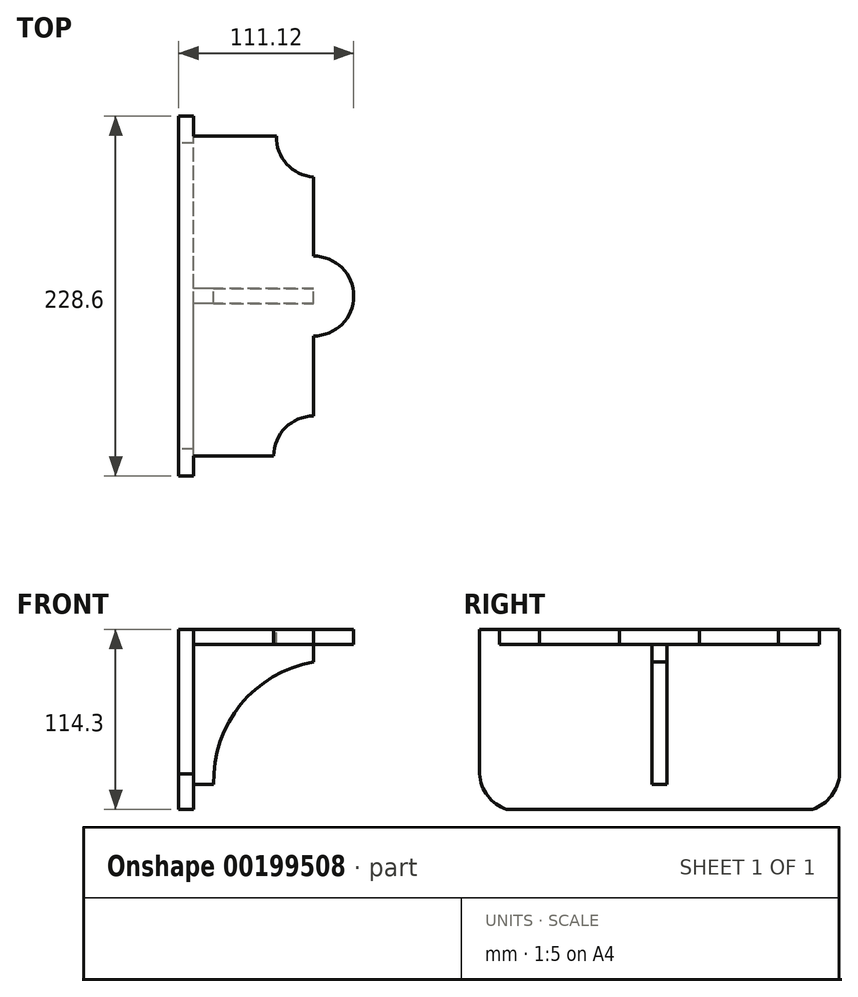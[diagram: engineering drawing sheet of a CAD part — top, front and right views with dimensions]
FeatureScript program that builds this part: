
annotation { "Feature Type Name" : "Feature", "Feature Type Description" : "" }
export const myFeature = defineFeature(function(context is Context, id is Id, definition is map)
    precondition{}
    {
        {
            var Q0;
            Q0=qCreatedBy(makeId("Right.planeOp"),FACE);
            var sketch = newSketch(context, id + "F0", { "sketchPlane" : qUnion([Q0])});
            skCircle(sketch, "E0", {"center": v(-124.94, 46.26) * mm, "radius": 10.4 * mm});
            skCircle(sketch, "E1", {"center": v(-124.94, 46.26) * mm, "radius": 31.75 * mm});
            skLineSegment(sketch, "E2", {"start": v(-122, 77.88) * mm, "end": v(-17.23, 77.88) * mm});
            skLineSegment(sketch, "E3", {"start": v(-118.16, 15.24) * mm, "end": v(-0.71, 15.24) * mm});
            skArc(sketch, "E4", {"start": v(-17.23, 77.88) * mm, "mid": v(-11.77, 60.6) * mm, "end": v(2.24, 49.13) * mm});
            skPoint(sketch, "E5.end.orphan", {"position": v(14.51, 77.88) * mm});
            skLineSegment(sketch, "E6", {"start": v(0.91, 49.73) * mm, "end": v(-0.71, 50.12) * mm});
            skLineSegment(sketch, "E7", {"start": v(-0.71, 50.12) * mm, "end": v(-0.71, 15.24) * mm});
            skPoint(sketch, "E8.orphan", {"position": v(-98.12, -71.85) * mm});
            skPoint(sketch, "E9", {"position": v(-37.66, -95.52) * mm});
            skLineSegment(sketch, "E10.bottom", {"start": v(-14.08, -27.06) * mm, "end": v(122.44, -27.06) * mm});
            skLineSegment(sketch, "E10.top", {"start": v(-14.08, -93.74) * mm, "end": v(122.44, -93.74) * mm});
            skLineSegment(sketch, "E10.left", {"start": v(-14.08, -27.06) * mm, "end": v(-14.08, -93.74) * mm});
            skLineSegment(sketch, "E10.right", {"start": v(122.44, -27.06) * mm, "end": v(122.44, -93.74) * mm});
            skArc(sketch, "E11", {"start": v(-98.28, -181.01) * mm, "mid": v(-129.26, -187.55) * mm, "end": v(-97.65, -185.78) * mm});
            skCircle(sketch, "E12", {"center": v(-113.52, -185.46) * mm, "radius": 31.75 * mm});
            skCircle(sketch, "E13", {"center": v(-37.32, -185.46) * mm, "radius": 11.11 * mm});
            skArc(sketch, "E14", {"start": v(-37.32, -210.86) * mm, "mid": v(-11.92, -185.46) * mm, "end": v(-37.32, -160.06) * mm});
            skLineSegment(sketch, "E15", {"start": v(-37.32, -160.06) * mm, "end": v(-94.47, -160.06) * mm});
            skLineSegment(sketch, "E16", {"start": v(-37.32, -210.86) * mm, "end": v(-94.47, -210.86) * mm});
            skLineSegment(sketch, "E17", {"start": v(-88.76, -181.01) * mm, "end": v(-98.28, -181.01) * mm});
            skLineSegment(sketch, "E18.MirrorCS", {"start": v(-88.76, -185.78) * mm, "end": v(-98.28, -185.78) * mm});
            skLineSegment(sketch, "E19", {"start": v(-88.76, -181.01) * mm, "end": v(-88.76, -185.78) * mm});
            skPoint(sketch, "E20.end.orphan", {"position": v(-40.1, -44.78) * mm});
            skPoint(sketch, "E20.start.orphan", {"position": v(-37.66, -44.78) * mm});
            skLineSegment(sketch, "E21", {"start": v(43.46, -93.74) * mm, "end": v(4.97, -27.06) * mm});
            skLineSegment(sketch, "E22", {"start": v(64.9, -93.74) * mm, "end": v(103.4, -27.06) * mm});
            skCircle(sketch, "E23", {"center": v(-494, 168.25) * mm, "radius": 73.03 * mm});
            skCircle(sketch, "E24", {"center": v(-494, 168.25) * mm, "radius": 38.1 * mm});
            skCircle(sketch, "E25", {"center": v(-494, 223.53) * mm, "radius": 7.94 * mm});
            skCircle(sketch, "E26", {"center": v(-530.58, 210.96) * mm, "radius": 7.94 * mm});
            skCircle(sketch, "E27", {"center": v(-550.67, 168.25) * mm, "radius": 7.94 * mm});
            skCircle(sketch, "E28", {"center": v(-528.76, 129.25) * mm, "radius": 7.94 * mm});
            skCircle(sketch, "E29.MirrorC", {"center": v(-457.4, 210.96) * mm, "radius": 7.94 * mm});
            skCircle(sketch, "E30.MirrorC", {"center": v(-437.33, 168.25) * mm, "radius": 7.94 * mm});
            skCircle(sketch, "E31.MirrorC", {"center": v(-459.23, 129.25) * mm, "radius": 7.94 * mm});
            skLineSegment(sketch, "E32.bottom", {"start": v(-629.68, -40.5) * mm, "end": v(-515.38, -40.5) * mm});
            skLineSegment(sketch, "E32.top", {"start": v(-629.68, -154.8) * mm, "end": v(-515.38, -154.8) * mm});
            skLineSegment(sketch, "E32.left", {"start": v(-629.68, -40.5) * mm, "end": v(-629.68, -154.8) * mm});
            skLineSegment(sketch, "E32.right", {"start": v(-515.38, -40.5) * mm, "end": v(-515.38, -154.8) * mm});
            skPoint(sketch, "E33", {"position": v(-515.38, -97.64) * mm});
            skPoint(sketch, "E34", {"position": v(-572.53, -40.5) * mm});
            skLineSegment(sketch, "E35", {"start": v(-572.53, -40.5) * mm, "end": v(-572.53, -154.8) * mm});
            skLineSegment(sketch, "E36", {"start": v(-515.38, -97.64) * mm, "end": v(-629.68, -97.64) * mm});
            skPoint(sketch, "E37.orphan", {"position": v(-629.68, -154.8) * mm});
            skPoint(sketch, "E38.MirrorCS.start.orphan", {"position": v(-515.38, -40.5) * mm});
            skPoint(sketch, "E39.MirrorCS.start.orphan", {"position": v(-515.38, -154.8) * mm});
            skLineSegment(sketch, "E40", {"start": v(-572.53, -59.48) * mm, "end": v(-610.7, -97.64) * mm});
            skLineSegment(sketch, "E41.MirrorCS", {"start": v(-572.53, -59.48) * mm, "end": v(-534.37, -97.64) * mm});
            skLineSegment(sketch, "E42.MirrorCS", {"start": v(-572.53, -135.81) * mm, "end": v(-610.7, -97.64) * mm});
            skLineSegment(sketch, "E43.MirrorCS", {"start": v(-572.53, -135.81) * mm, "end": v(-534.37, -97.64) * mm});
            skLineSegment(sketch, "E44", {"start": v(-515.38, -40.5) * mm, "end": v(-477.28, -62.5) * mm});
            skLineSegment(sketch, "E45", {"start": v(-477.28, -62.5) * mm, "end": v(-477.28, -81.14) * mm});
            skLineSegment(sketch, "E46", {"start": v(-477.28, -81.14) * mm, "end": v(-515.38, -81.14) * mm});
            skLineSegment(sketch, "E47", {"start": v(-477.28, -81.14) * mm, "end": v(-477.28, -26.83) * mm});
            skLineSegment(sketch, "E48.MirrorCS", {"start": v(-477.28, -114.15) * mm, "end": v(-515.38, -114.15) * mm});
            skLineSegment(sketch, "E49.MirrorCS", {"start": v(-515.38, -154.8) * mm, "end": v(-477.28, -132.8) * mm});
            skLineSegment(sketch, "E50.MirrorCS", {"start": v(-667.78, -81.14) * mm, "end": v(-629.68, -81.14) * mm});
            skLineSegment(sketch, "E51.MirrorCS", {"start": v(-629.68, -40.5) * mm, "end": v(-667.78, -62.5) * mm});
            skLineSegment(sketch, "E52.MirrorCS", {"start": v(-667.78, -81.14) * mm, "end": v(-667.78, -62.5) * mm});
            skLineSegment(sketch, "E53.MirrorCS", {"start": v(-667.78, -114.15) * mm, "end": v(-629.68, -114.15) * mm});
            skLineSegment(sketch, "E54.MirrorCS", {"start": v(-667.78, -114.45) * mm, "end": v(-667.78, -132.8) * mm});
            skLineSegment(sketch, "E55", {"start": v(-477.28, -114.15) * mm, "end": v(-477.28, -132.8) * mm});
            skLineSegment(sketch, "E56", {"start": v(-667.78, -132.8) * mm, "end": v(-629.68, -154.8) * mm});
            skLineSegment(sketch, "E57", {"start": v(-667.78, -114.15) * mm, "end": v(-667.78, -114.47) * mm});
            skLineSegment(sketch, "E58.bottom", {"start": v(-407.73, 102.8) * mm, "end": v(-279.92, 102.8) * mm});
            skLineSegment(sketch, "E58.top", {"start": v(-407.73, -11.5) * mm, "end": v(-279.92, -11.5) * mm});
            skLineSegment(sketch, "E58.left", {"start": v(-407.73, 102.8) * mm, "end": v(-407.73, -11.5) * mm});
            skLineSegment(sketch, "E58.right", {"start": v(-279.92, 102.8) * mm, "end": v(-279.92, -11.5) * mm});
            skLineSegment(sketch, "E59", {"start": v(-407.73, 102.8) * mm, "end": v(-440.64, 45.66) * mm});
            skLineSegment(sketch, "E60", {"start": v(-440.64, 45.66) * mm, "end": v(-407.73, -11.5) * mm});
            skLineSegment(sketch, "E61", {"start": v(-279.92, 102.8) * mm, "end": v(-250.14, 45.66) * mm});
            skLineSegment(sketch, "E62", {"start": v(-250.14, 45.66) * mm, "end": v(-279.92, -11.5) * mm});
            skLineSegment(sketch, "E63.bottom", {"start": v(-358.1, 115.5) * mm, "end": v(-326.34, 115.5) * mm});
            skLineSegment(sketch, "E63.top", {"start": v(-358.1, -24.2) * mm, "end": v(-326.34, -24.2) * mm});
            skLineSegment(sketch, "E63.left", {"start": v(-358.1, 115.5) * mm, "end": v(-358.1, -24.2) * mm});
            skLineSegment(sketch, "E63.right", {"start": v(-326.34, 115.5) * mm, "end": v(-326.34, -24.2) * mm});
            skLineSegment(sketch, "E64.bottom", {"start": v(-405.33, 64.7) * mm, "end": v(-351.35, 64.7) * mm});
            skLineSegment(sketch, "E64.top", {"start": v(-405.33, 26.6) * mm, "end": v(-351.35, 26.6) * mm});
            skLineSegment(sketch, "E64.left", {"start": v(-405.33, 64.7) * mm, "end": v(-405.33, 26.6) * mm});
            skLineSegment(sketch, "E64.right", {"start": v(-351.35, 64.7) * mm, "end": v(-351.35, 26.6) * mm});
            skLineSegment(sketch, "E65.MirrorCS", {"start": v(-285.46, 64.7) * mm, "end": v(-339.43, 64.7) * mm});
            skLineSegment(sketch, "E66.MirrorCS", {"start": v(-339.43, 64.7) * mm, "end": v(-339.43, 26.6) * mm});
            skLineSegment(sketch, "E67.MirrorCS", {"start": v(-285.46, 26.6) * mm, "end": v(-339.43, 26.6) * mm});
            skLineSegment(sketch, "E68.MirrorCS", {"start": v(-285.46, 64.7) * mm, "end": v(-285.46, 26.6) * mm});
            skLineSegment(sketch, "E69", {"start": v(-407.73, 102.8) * mm, "end": v(-397.88, 115.48) * mm});
            skLineSegment(sketch, "E70", {"start": v(-397.88, 115.48) * mm, "end": v(-389.84, 115.5) * mm});
            skLineSegment(sketch, "E71", {"start": v(-389.84, 115.5) * mm, "end": v(-389.84, 102.8) * mm});
            skLineSegment(sketch, "E72.MirrorCS", {"start": v(-300.94, 115.5) * mm, "end": v(-300.94, 102.8) * mm});
            skLineSegment(sketch, "E73.MirrorCS", {"start": v(-279.92, 102.8) * mm, "end": v(-292.62, 115.5) * mm});
            skLineSegment(sketch, "E74.MirrorCS", {"start": v(-292.62, 115.5) * mm, "end": v(-300.94, 115.5) * mm});
            skLineSegment(sketch, "E75.MirrorCS", {"start": v(-407.73, -11.5) * mm, "end": v(-397.99, -24.2) * mm});
            skLineSegment(sketch, "E76.MirrorCS", {"start": v(-397.99, -24.2) * mm, "end": v(-389.67, -24.2) * mm});
            skPoint(sketch, "E77", {"position": v(-326.34, 102.8) * mm});
            skLineSegment(sketch, "E78", {"start": v(-389.67, -24.2) * mm, "end": v(-389.67, -11.5) * mm});
            skPoint(sketch, "E79", {"position": v(-358.1, -11.5) * mm});
            skPoint(sketch, "E80.startSnap0", {"position": v(-342.22, 115.5) * mm});
            skLineSegment(sketch, "E81.MirrorCS", {"start": v(-286.45, -24.2) * mm, "end": v(-294.76, -24.2) * mm});
            skLineSegment(sketch, "E82.MirrorCS", {"start": v(-279.92, -11.5) * mm, "end": v(-286.45, -24.2) * mm});
            skLineSegment(sketch, "E83.MirrorCS", {"start": v(-294.76, -24.2) * mm, "end": v(-294.76, -11.5) * mm});
            skCircle(sketch, "E84", {"center": v(-850.31, 154.76) * mm, "radius": 63.5 * mm});
            skCircle(sketch, "E85", {"center": v(-850.31, 154.76) * mm, "radius": 44.45 * mm});
            skCircle(sketch, "E86", {"center": v(-926.51, 149.48) * mm, "radius": 40.81 * mm});
            skCircle(sketch, "E87.MirrorC", {"center": v(-774.11, 149.48) * mm, "radius": 40.81 * mm});
            skCircle(sketch, "E88", {"center": v(-926.51, 149.48) * mm, "radius": 12.7 * mm});
            skCircle(sketch, "E89.MirrorC", {"center": v(-774.11, 149.48) * mm, "radius": 12.7 * mm});
            skCircle(sketch, "E90", {"center": v(-503.59, -297.02) * mm, "radius": 19.05 * mm});
            skCircle(sketch, "E91", {"center": v(-503.59, -297.02) * mm, "radius": 31.75 * mm});
            skLineSegment(sketch, "E92", {"start": v(-503.59, -328.77) * mm, "end": v(-617.89, -328.77) * mm});
            skLineSegment(sketch, "E93", {"start": v(-503.59, -265.27) * mm, "end": v(-617.89, -265.27) * mm});
            skArc(sketch, "E94", {"start": v(-652.7, -239.87) * mm, "mid": v(-642.34, -262.23) * mm, "end": v(-617.89, -265.27) * mm});
            skArc(sketch, "E95.MirrorCS", {"start": v(-652.7, -354.17) * mm, "mid": v(-642.34, -331.81) * mm, "end": v(-617.89, -328.77) * mm});
            skLineSegment(sketch, "E96", {"start": v(-652.7, -239.87) * mm, "end": v(-672.55, -239.87) * mm});
            skLineSegment(sketch, "E97", {"start": v(-672.55, -239.87) * mm, "end": v(-680.33, -247.66) * mm});
            skLineSegment(sketch, "E98", {"start": v(-680.33, -247.66) * mm, "end": v(-680.33, -266.05) * mm});
            skLineSegment(sketch, "E99", {"start": v(-680.33, -247.66) * mm, "end": v(-680.33, -223.63) * mm});
            skLineSegment(sketch, "E100.MirrorCS", {"start": v(-680.33, -346.39) * mm, "end": v(-680.33, -328) * mm});
            skLineSegment(sketch, "E101.MirrorCS", {"start": v(-672.55, -354.17) * mm, "end": v(-680.33, -346.39) * mm});
            skLineSegment(sketch, "E102.MirrorCS", {"start": v(-652.7, -354.17) * mm, "end": v(-672.55, -354.17) * mm});
            skArc(sketch, "E103", {"start": v(-680.33, -328) * mm, "mid": v(-655.56, -297.02) * mm, "end": v(-680.33, -266.05) * mm});
            skCircle(sketch, "E104", {"center": v(-1098.37, -60.28) * mm, "radius": 15.88 * mm});
            skCircle(sketch, "E105", {"center": v(-1053.92, -60.68) * mm, "radius": 15.88 * mm});
            skCircle(sketch, "E106", {"center": v(-1053.92, -60.68) * mm, "radius": 27.2 * mm});
            skLineSegment(sketch, "E107", {"start": v(-1098.37, -60.28) * mm, "end": v(-1098.37, -34.09) * mm});
            skLineSegment(sketch, "E108", {"start": v(-1053.92, -60.68) * mm, "end": v(-1053.92, -33.49) * mm});
            skLineSegment(sketch, "E109", {"start": v(-1053.92, -33.49) * mm, "end": v(-1098.37, -33.49) * mm});
            skCircle(sketch, "E110", {"center": v(-1098.37, -60.28) * mm, "radius": 27.5 * mm});
            skArc(sketch, "E111", {"start": v(-1125.2, -66.3) * mm, "mid": v(-1154.07, -82.44) * mm, "end": v(-1138.06, -111.39) * mm});
            skLineSegment(sketch, "E112.bottom", {"start": v(-979.8, 459.56) * mm, "end": v(-827.4, 459.56) * mm});
            skLineSegment(sketch, "E112.top", {"start": v(-979.8, 357.96) * mm, "end": v(-827.4, 357.96) * mm});
            skLineSegment(sketch, "E112.left", {"start": v(-979.8, 459.56) * mm, "end": v(-979.8, 357.96) * mm});
            skLineSegment(sketch, "E112.right", {"start": v(-827.4, 459.56) * mm, "end": v(-827.4, 357.96) * mm});
            skLineSegment(sketch, "E113.bottom", {"start": v(-979.58, 437.13) * mm, "end": v(-827.18, 437.13) * mm});
            skLineSegment(sketch, "E113.top", {"start": v(-979.58, 373.63) * mm, "end": v(-827.18, 373.63) * mm});
            skLineSegment(sketch, "E113.left", {"start": v(-979.58, 437.13) * mm, "end": v(-979.58, 373.63) * mm});
            skLineSegment(sketch, "E113.right", {"start": v(-827.18, 437.13) * mm, "end": v(-827.18, 373.63) * mm});
            skCircle(sketch, "E114", {"center": v(-906.04, 408.76) * mm, "radius": 12.67 * mm});
            skLineSegment(sketch, "E115.bottom", {"start": v(-1247.26, 465.3) * mm, "end": v(-1129.79, 465.3) * mm});
            skLineSegment(sketch, "E115.top", {"start": v(-1247.26, 331.95) * mm, "end": v(-1129.79, 331.95) * mm});
            skLineSegment(sketch, "E115.left", {"start": v(-1247.26, 465.3) * mm, "end": v(-1247.26, 331.95) * mm});
            skLineSegment(sketch, "E115.right", {"start": v(-1129.79, 465.3) * mm, "end": v(-1129.79, 331.95) * mm});
            skCircle(sketch, "E116", {"center": v(-1215.51, 433.56) * mm, "radius": 10.32 * mm});
            skCircle(sketch, "E117", {"center": v(-1161.54, 433.56) * mm, "radius": 10.32 * mm});
            skLineSegment(sketch, "E118.bottom", {"start": v(-1247.26, 400.21) * mm, "end": v(-1129.79, 400.21) * mm});
            skLineSegment(sketch, "E118.top", {"start": v(-1247.26, 387.53) * mm, "end": v(-1129.79, 387.53) * mm});
            skLineSegment(sketch, "E118.left", {"start": v(-1247.26, 400.21) * mm, "end": v(-1247.26, 387.53) * mm});
            skLineSegment(sketch, "E118.right", {"start": v(-1129.79, 400.21) * mm, "end": v(-1129.79, 387.53) * mm});
            skLineSegment(sketch, "E119.bottom", {"start": v(-1247.26, 344.65) * mm, "end": v(-1129.79, 344.65) * mm});
            skLineSegment(sketch, "E119.left", {"start": v(-1247.26, 344.65) * mm, "end": v(-1247.26, 331.95) * mm});
            skLineSegment(sketch, "E119.right", {"start": v(-1129.79, 344.65) * mm, "end": v(-1129.79, 331.95) * mm});
            skLineSegment(sketch, "E120.bottom", {"start": v(-586.94, 445.97) * mm, "end": v(-523.44, 445.97) * mm});
            skLineSegment(sketch, "E120.top", {"start": v(-586.94, 328.5) * mm, "end": v(-523.44, 328.5) * mm});
            skLineSegment(sketch, "E120.left", {"start": v(-586.94, 445.97) * mm, "end": v(-586.94, 328.5) * mm});
            skLineSegment(sketch, "E120.right", {"start": v(-523.44, 445.97) * mm, "end": v(-523.44, 328.5) * mm});
            skLineSegment(sketch, "E121.bottom", {"start": v(-577.42, 328.5) * mm, "end": v(-532.97, 328.5) * mm});
            skLineSegment(sketch, "E121.top", {"start": v(-577.42, 385.64) * mm, "end": v(-532.97, 385.64) * mm});
            skLineSegment(sketch, "E121.left", {"start": v(-577.42, 328.5) * mm, "end": v(-577.42, 385.64) * mm});
            skLineSegment(sketch, "E121.right", {"start": v(-532.97, 328.5) * mm, "end": v(-532.97, 385.64) * mm});
            skLineSegment(sketch, "E122.top", {"start": v(-577.42, 445.97) * mm, "end": v(-532.97, 445.97) * mm});
            skLineSegment(sketch, "E122.left", {"start": v(-577.42, 385.64) * mm, "end": v(-577.42, 445.97) * mm});
            skLineSegment(sketch, "E122.right", {"start": v(-532.97, 385.64) * mm, "end": v(-532.97, 445.97) * mm});
            skCircle(sketch, "E123", {"center": v(-555.2, 360.24) * mm, "radius": 9.53 * mm});
            skCircle(sketch, "E124", {"center": v(-555.2, 415.8) * mm, "radius": 9.53 * mm});
            skCircle(sketch, "E125", {"center": v(-287.16, -126.2) * mm, "radius": 15.88 * mm});
            skCircle(sketch, "E126", {"center": v(-331.61, -125.53) * mm, "radius": 15.88 * mm});
            skArc(sketch, "E127", {"start": v(-379.88, -217.46) * mm, "mid": v(-354.98, -196.07) * mm, "end": v(-362.32, -164.08) * mm});
            skArc(sketch, "E128", {"start": v(-332.46, -103.23) * mm, "mid": v(-356.85, -130.81) * mm, "end": v(-359.42, -167.55) * mm});
            skLineSegment(sketch, "E129", {"start": v(-379.88, -217.46) * mm, "end": v(-379.88, -230.16) * mm});
            skLineSegment(sketch, "E130", {"start": v(-379.88, -230.16) * mm, "end": v(-319.55, -290.48) * mm});
            skLineSegment(sketch, "E131", {"start": v(-319.55, -290.48) * mm, "end": v(-300.5, -290.48) * mm});
            skLineSegment(sketch, "E132", {"start": v(-319.55, -290.48) * mm, "end": v(-454.22, -290.48) * mm});
            skLineSegment(sketch, "E133", {"start": v(-310.03, -85.84) * mm, "end": v(-310.03, -290.48) * mm});
            skLineSegment(sketch, "E134", {"start": v(-367.58, -224.04) * mm, "end": v(-156.94, -224.04) * mm});
            skCircle(sketch, "E135", {"center": v(-310.03, -224.04) * mm, "radius": 31.75 * mm});
            skCircle(sketch, "E136", {"center": v(-341.78, -224.04) * mm, "radius": 7.94 * mm});
            skCircle(sketch, "E137.MirrorC", {"center": v(-278.28, -224.04) * mm, "radius": 7.94 * mm});
            skLineSegment(sketch, "E138.MirrorCS", {"start": v(-240.18, -217.46) * mm, "end": v(-240.18, -230.16) * mm});
            skArc(sketch, "E139.MirrorCS", {"start": v(-240.18, -217.46) * mm, "mid": v(-265.07, -196.07) * mm, "end": v(-257.74, -164.08) * mm});
            skArc(sketch, "E140.MirrorCS", {"start": v(-287.6, -103.23) * mm, "mid": v(-263.2, -130.81) * mm, "end": v(-260.64, -167.55) * mm});
            skLineSegment(sketch, "E141.MirrorCS", {"start": v(-240.18, -230.16) * mm, "end": v(-300.5, -290.48) * mm});
            skLineSegment(sketch, "E142", {"start": v(-332.46, -103.23) * mm, "end": v(-287.6, -103.23) * mm});
            skLineSegment(sketch, "E143.bottom", {"start": v(-214.58, 668.47) * mm, "end": v(-46.2, 668.47) * mm});
            skLineSegment(sketch, "E143.top", {"start": v(-214.58, 454.06) * mm, "end": v(-46.2, 454.06) * mm});
            skLineSegment(sketch, "E143.left", {"start": v(-214.58, 668.47) * mm, "end": v(-214.58, 454.06) * mm});
            skLineSegment(sketch, "E143.right", {"start": v(-46.2, 668.47) * mm, "end": v(-46.2, 454.06) * mm});
            skLineSegment(sketch, "E144", {"start": v(-214.58, 454.06) * mm, "end": v(-168.96, 422.3) * mm});
            skLineSegment(sketch, "E145", {"start": v(-168.96, 422.3) * mm, "end": v(-153.72, 422.3) * mm});
            skLineSegment(sketch, "E146", {"start": v(-153.72, 422.3) * mm, "end": v(-153.72, 511.2) * mm});
            skLineSegment(sketch, "E147", {"start": v(-153.72, 511.2) * mm, "end": v(-110.84, 511.2) * mm});
            skLineSegment(sketch, "E148", {"start": v(-110.84, 511.2) * mm, "end": v(-110.84, 422.3) * mm});
            skLineSegment(sketch, "E149", {"start": v(-110.84, 422.3) * mm, "end": v(-94.8, 422.3) * mm});
            skLineSegment(sketch, "E150", {"start": v(-94.8, 422.3) * mm, "end": v(-46.2, 454.06) * mm});
            skLineSegment(sketch, "E151.top", {"start": v(-214.58, 614.67) * mm, "end": v(-46.2, 614.67) * mm});
            skLineSegment(sketch, "E151.left", {"start": v(-214.58, 668.47) * mm, "end": v(-214.58, 614.67) * mm});
            skLineSegment(sketch, "E151.right", {"start": v(-46.2, 668.47) * mm, "end": v(-46.2, 614.67) * mm});
            skLineSegment(sketch, "E152.bottom", {"start": v(-214.58, 668.47) * mm, "end": v(-195.53, 668.47) * mm});
            skLineSegment(sketch, "E152.top", {"start": v(-214.58, 614.67) * mm, "end": v(-195.53, 614.67) * mm});
            skLineSegment(sketch, "E152.right", {"start": v(-195.53, 668.47) * mm, "end": v(-195.53, 614.67) * mm});
            skLineSegment(sketch, "E153.bottom", {"start": v(-46.2, 668.47) * mm, "end": v(-65.25, 668.47) * mm});
            skLineSegment(sketch, "E153.top", {"start": v(-46.2, 614.67) * mm, "end": v(-65.25, 614.67) * mm});
            skLineSegment(sketch, "E153.right", {"start": v(-65.25, 668.47) * mm, "end": v(-65.25, 614.67) * mm});
            skLineSegment(sketch, "E154.bottom", {"start": v(94.57, 2146.5) * mm, "end": v(145.37, 2146.5) * mm});
            skLineSegment(sketch, "E154.top", {"start": v(94.57, 2083.5) * mm, "end": v(145.37, 2083.5) * mm});
            skLineSegment(sketch, "E154.left", {"start": v(94.57, 2146.5) * mm, "end": v(94.57, 2083.5) * mm});
            skLineSegment(sketch, "E154.right", {"start": v(145.37, 2146.5) * mm, "end": v(145.37, 2083.5) * mm});
            skCircle(sketch, "E155", {"center": v(120.41, 2057.6) * mm, "radius": 19.05 * mm});
            skCircle(sketch, "E156", {"center": v(120.41, 2057.6) * mm, "radius": 34.93 * mm});
            skCircle(sketch, "E157", {"center": v(118.76, 2134.57) * mm, "radius": 8.44 * mm});
            skCircle(sketch, "E158", {"center": v(469.6, 2753.56) * mm, "radius": 25.4 * mm});
            skEllipse(sketch, "E159", {"center": v(458.53, 2754.64) * mm, "majorRadius": 3.7 * mm, "minorRadius": 2.2 * mm, "majorAxis": v(-0.68, 0.74)});
            skEllipse(sketch, "E160", {"center": v(480.48, 2753.2) * mm, "majorRadius": 3.03 * mm, "minorRadius": 2.16 * mm, "majorAxis": v(-0.7, -0.7)});
            skEllipse(sketch, "E161", {"center": v(475.16, 2758.74) * mm, "majorRadius": 3.6 * mm, "minorRadius": 2.56 * mm, "majorAxis": v(-0.44, -0.9)});
            skEllipse(sketch, "E162", {"center": v(465.32, 2759.1) * mm, "majorRadius": 3.64 * mm, "minorRadius": 2.38 * mm, "majorAxis": v(0.3, -0.95)});
            skText(sketch, "E163", { "text": "O", "fontName": "Tinos-Bold.ttf"});
            skLineSegment(sketch, "E164", {"start": v(469.6, 2753.56) * mm, "end": v(470.66, 2806.38) * mm, "construction": true});
            skText(sketch, "E165", { "text": "DOVER", "fontName": "Tinos-Regular.ttf"});
            skText(sketch, "E166", { "text": "571-265-7354  Herndon, VA", "fontName": "Tinos-Regular.ttf"});
            skFitSpline(sketch, "E167", {"points": [v(468.33, 2752.37) * mm, v(462.16, 2749.72) * mm, v(459.96, 2743.43) * mm, v(463.3, 2739.15) * mm, v(469.52, 2741.1) * mm, v(476.45, 2739.73) * mm, v(480.1, 2744.96) * mm, v(475.94, 2749.92) * mm, v(470.78, 2752.37) * mm, v(468.33, 2752.37) * mm]});
            skCircle(sketch, "E168", {"center": v(470.19, 2783.04) * mm, "radius": 2.54 * mm});
            skArc(sketch, "E169", {"start": v(475.3, 2778.31) * mm, "mid": v(470.33, 2790) * mm, "end": v(464.9, 2778.52) * mm});
            skArc(sketch, "E170", {"start": v(461.07, 2777.49) * mm, "mid": v(462.38, 2780.42) * mm, "end": v(463.24, 2783.51) * mm});
            skArc(sketch, "E171.MirrorCS", {"start": v(479.08, 2777.12) * mm, "mid": v(477.88, 2780.1) * mm, "end": v(477.15, 2783.23) * mm});
            skLineSegment(sketch, "E172", {"start": v(437.74, 2190.65) * mm, "end": v(437.7, 2190.65) * mm});
            skLineSegment(sketch, "E173", {"start": v(437.7, 2190.65) * mm, "end": v(437.69, 2190.64) * mm});
            skCircle(sketch, "E174", {"center": v(115.69, 2555.08) * mm, "radius": 15.87 * mm});
            skCircle(sketch, "E175", {"center": v(160.14, 2529.17) * mm, "radius": 15.87 * mm});
            skPoint(sketch, "E176", {"position": v(119.74, 2539.73) * mm});
            skPoint(sketch, "E177", {"position": v(157.28, 2544.78) * mm});
            skCircle(sketch, "E178", {"center": v(83.94, 2500.6) * mm, "radius": 7.94 * mm});
            skCircle(sketch, "E179", {"center": v(191.89, 2500.6) * mm, "radius": 7.94 * mm});
            skLineSegment(sketch, "E180", {"start": v(83.94, 2500.6) * mm, "end": v(227.7, 2500.6) * mm});
            skLineSegment(sketch, "E181", {"start": v(227.7, 2500.6) * mm, "end": v(-16.12, 2500.6) * mm});
            skLineSegment(sketch, "E182", {"start": v(-16.12, 2500.6) * mm, "end": v(260.1, 2500.6) * mm});
            skCircle(sketch, "E183", {"center": v(140.68, 2500.6) * mm, "radius": 31.75 * mm});
            skLineSegment(sketch, "E184", {"start": v(139.75, 2482.93) * mm, "end": v(139.75, 2446.62) * mm});
            skLineSegment(sketch, "E185", {"start": v(139.75, 2446.62) * mm, "end": v(139.75, 2327.9) * mm});
            skCircle(sketch, "E186", {"center": v(139.75, 2446.62) * mm, "radius": 7.94 * mm});
            skLineSegment(sketch, "E187", {"start": v(101.44, 2529.17) * mm, "end": v(256.71, 2529.17) * mm});
            skLineSegment(sketch, "E188", {"start": v(99.16, 2577.08) * mm, "end": v(138.96, 2577.08) * mm});
            skArc(sketch, "E189", {"start": v(99.16, 2577.08) * mm, "mid": v(65.79, 2563.37) * mm, "end": v(51.7, 2530.15) * mm});
            skLineSegment(sketch, "E190", {"start": v(25.37, 2504.02) * mm, "end": v(25.37, 2491.32) * mm});
            skArc(sketch, "E191", {"start": v(25.37, 2504.02) * mm, "mid": v(42.75, 2512.84) * mm, "end": v(51.7, 2530.15) * mm});
            skLineSegment(sketch, "E192", {"start": v(138.96, 2577.08) * mm, "end": v(139.75, 2557.78) * mm});
            skLineSegment(sketch, "E193.MirrorCS", {"start": v(185.28, 2577.46) * mm, "end": v(138.94, 2576.88) * mm});
            skArc(sketch, "E194.MirrorCS", {"start": v(185.28, 2577.46) * mm, "mid": v(215.64, 2561.98) * mm, "end": v(227.8, 2530.15) * mm});
            skArc(sketch, "E195.MirrorCS", {"start": v(254.13, 2504.02) * mm, "mid": v(236.75, 2512.84) * mm, "end": v(227.8, 2530.15) * mm});
            skLineSegment(sketch, "E196.MirrorCS", {"start": v(254.13, 2504.02) * mm, "end": v(254.13, 2491.32) * mm});
            skLineSegment(sketch, "E197.MirrorCS", {"start": v(140.53, 2557.78) * mm, "end": v(139.75, 2557.78) * mm});
            skLineSegment(sketch, "E198", {"start": v(25.37, 2491.32) * mm, "end": v(126.84, 2341.77) * mm});
            skLineSegment(sketch, "E199", {"start": v(126.84, 2341.77) * mm, "end": v(6.72, 2364.77) * mm});
            skLineSegment(sketch, "E200.MirrorCS", {"start": v(254.13, 2491.32) * mm, "end": v(152.66, 2341.77) * mm});
            skLineSegment(sketch, "E201", {"start": v(126.84, 2341.77) * mm, "end": v(152.66, 2341.77) * mm});
            skLineSegment(sketch, "E202.bottom", {"start": v(1141.88, 2377.35) * mm, "end": v(1370.48, 2377.35) * mm});
            skLineSegment(sketch, "E202.top", {"start": v(1159.09, 2263.05) * mm, "end": v(1353.28, 2263.05) * mm});
            skLineSegment(sketch, "E202.left", {"start": v(1141.88, 2377.35) * mm, "end": v(1141.88, 2285.53) * mm});
            skLineSegment(sketch, "E202.right", {"start": v(1370.48, 2377.35) * mm, "end": v(1370.48, 2285.53) * mm});
            skArc(sketch, "E203", {"start": v(1141.88, 2288.68) * mm, "mid": v(1146.14, 2272.95) * mm, "end": v(1159.09, 2263.05) * mm});
            skArc(sketch, "E204.MirrorCS", {"start": v(1370.48, 2288.68) * mm, "mid": v(1366.22, 2272.95) * mm, "end": v(1353.28, 2263.05) * mm});
            skPoint(sketch, "E205.orphan", {"position": v(1370.48, 2263.05) * mm});
            skPoint(sketch, "E206.orphan", {"position": v(1141.88, 2263.05) * mm});
            const initialGuessF0  = {"E163": [0.46082, 2.82938, 1, 0, 0.00311], "E165": [0.45619, 2.76826, 1, 0, 0.00548], "E166": [0.44445, 2.79179, 1, 0, 0.00456]};
            skSetInitialGuess(sketch, initialGuessF0);
            skSolve(sketch);
        }
        {
            var Q0;
            {var subQ4=sQuery(id+"F0.wireOp",EDGE,"E202.bottom");Q0=makeQuery(id+"F0.imprint","IMPRINT",FACE,{"disambiguationData":[TD([[makeQuery(id+"F0.imprint","IMPRINT",EDGE,{"derivedFrom":subQ4}),-1.0]])]});}
            extrude(context, id + "F1", {"entities" : qUnion([Q0]), "depth" : 9.52 * mm});
        }
        {
            var Q0;
            Q0=makeQuery(id+"F1.opExtrude","SWEPT_FACE",FACE,{"disambiguationData":[OSD([sQuery(id+"F0.wireOp",EDGE,"E202.bottom")])]});
            var sketch = newSketch(context, id + "F2", { "sketchPlane" : qUnion([Q0])});
            skLineSegment(sketch, "E207.0", {"start": v(9.53, 1141.88) * mm, "end": v(9.53, 1370.48) * mm});
            skLineSegment(sketch, "E208", {"start": v(9.52, 1154.58) * mm, "end": v(60.33, 1154.58) * mm});
            skLineSegment(sketch, "E209", {"start": v(85.73, 1179.98) * mm, "end": v(85.73, 1230.78) * mm});
            skLineSegment(sketch, "E210", {"start": v(62.04, 1357.78) * mm, "end": v(9.52, 1357.78) * mm});
            skArc(sketch, "E211", {"start": v(85.73, 1230.78) * mm, "mid": v(111.13, 1256.18) * mm, "end": v(85.73, 1281.58) * mm});
            skArc(sketch, "E212", {"start": v(85.73, 1179.98) * mm, "mid": v(67.76, 1172.54) * mm, "end": v(60.33, 1154.58) * mm});
            skArc(sketch, "E213", {"start": v(62.04, 1357.78) * mm, "mid": v(68.63, 1339.98) * mm, "end": v(85.73, 1331.72) * mm});
            skPoint(sketch, "E214.orphan", {"position": v(85.73, 1357.78) * mm});
            skLineSegment(sketch, "E215.trimOffspring", {"start": v(85.73, 1281.58) * mm, "end": v(85.73, 1331.72) * mm});
            skSolve(sketch);
        }
        {
            var Q0;
            {var subQ1=sQuery(id+"F2.wireOp",EDGE,"E208");Q0=makeQuery(id+"F2.imprint","IMPRINT",FACE,{"disambiguationData":[TD([[makeQuery(id+"F2.imprint","IMPRINT",EDGE,{"derivedFrom":subQ1}),1.0]])]});}
            extrude(context, id + "F3", {"entities" : qUnion([Q0]), "operationType" : NewBodyOperationType.ADD, "oppositeDirection" : true, "depth" : 9.52 * mm});
        }
        {
            var Q0;
            Q0=makeQuery(id+"F3.opExtrude","CAP_FACE",FACE,{"disambiguationData":[OSD([sQuery(id+"F2.wireOp",EDGE,"E207.0"),sQuery(id+"F2.wireOp",EDGE,"E208"),sQuery(id+"F2.wireOp",EDGE,"E209"),sQuery(id+"F2.wireOp",EDGE,"E210"),sQuery(id+"F2.wireOp",EDGE,"E211"),sQuery(id+"F2.wireOp",EDGE,"E212"),sQuery(id+"F2.wireOp",EDGE,"E213"),sQuery(id+"F2.wireOp",EDGE,"E215.trimOffspring")])],"isStart":false});
            var sketch = newSketch(context, id + "F4", { "sketchPlane" : qUnion([Q0])});
            skLineSegment(sketch, "E216.0", {"start": v(85.73, -1251.42) * mm, "end": v(9.52, -1251.42) * mm});
            skLineSegment(sketch, "E217.0", {"start": v(85.73, -1260.95) * mm, "end": v(9.52, -1260.95) * mm});
            skLineSegment(sketch, "E218", {"start": v(85.73, -1251.42) * mm, "end": v(85.73, -1260.95) * mm});
            skPoint(sketch, "E219.orphan", {"position": v(111.13, -1256.18) * mm});
            skSolve(sketch);
        }
        {
            var Q0;
            {var subQ0=sQuery(id+"F4.wireOp",EDGE,"E216.0");Q0=makeQuery(id+"F4.imprint","IMPRINT",FACE,{"disambiguationData":[TD([[makeQuery(id+"F4.imprint","IMPRINT",EDGE,{"derivedFrom":subQ0}),1.0]])]});}
            extrude(context, id + "F5", {"entities" : qUnion([Q0]), "operationType" : NewBodyOperationType.ADD, "depth" : 88.9 * mm});
        }
        {
            var Q0;
            Q0=makeQuery(id+"F5.opExtrude","SWEPT_FACE",FACE,{"disambiguationData":[OSD([sQuery(id+"F4.wireOp",EDGE,"E217.0")])]});
            var sketch = newSketch(context, id + "F6", { "sketchPlane" : qUnion([Q0])});
            skArc(sketch, "E220", {"start": v(-22.27, 2278.92) * mm, "mid": v(-39.39, 2329.72) * mm, "end": v(-85.73, 2356.68) * mm});
            skPoint(sketch, "E221", {"position": v(-62.56, 2348.77) * mm});
            skPoint(sketch, "E222", {"position": v(-85.73, 2278.92) * mm});
            skSolve(sketch);
        }
        {
            var Q0;
            Q0=sQuery(id+"F6.wireOp",VERTEX,"E220.center");
            var Q1;
            Q1=makeQuery(id+"F1.opExtrude","SWEPT_BODY",BODY,{"disambiguationData":[OSD([sQuery(id+"F0.wireOp",EDGE,"E202.bottom"),sQuery(id+"F0.wireOp",EDGE,"E202.top"),sQuery(id+"F0.wireOp",EDGE,"E202.left"),sQuery(id+"F0.wireOp",EDGE,"E202.right"),sQuery(id+"F0.wireOp",EDGE,"E203"),sQuery(id+"F0.wireOp",EDGE,"E204.MirrorCS")])]});
            hole(context, id + "F7", {"style" : HoleStyle.SIMPLE, "endStyle" : HoleEndStyle.THROUGH, "holeDiameter" : 152.4 * mm, "locations" : qUnion([Q0]), "scope" : qUnion([Q1]), "isTappedThrough" : true});
        }
    });
